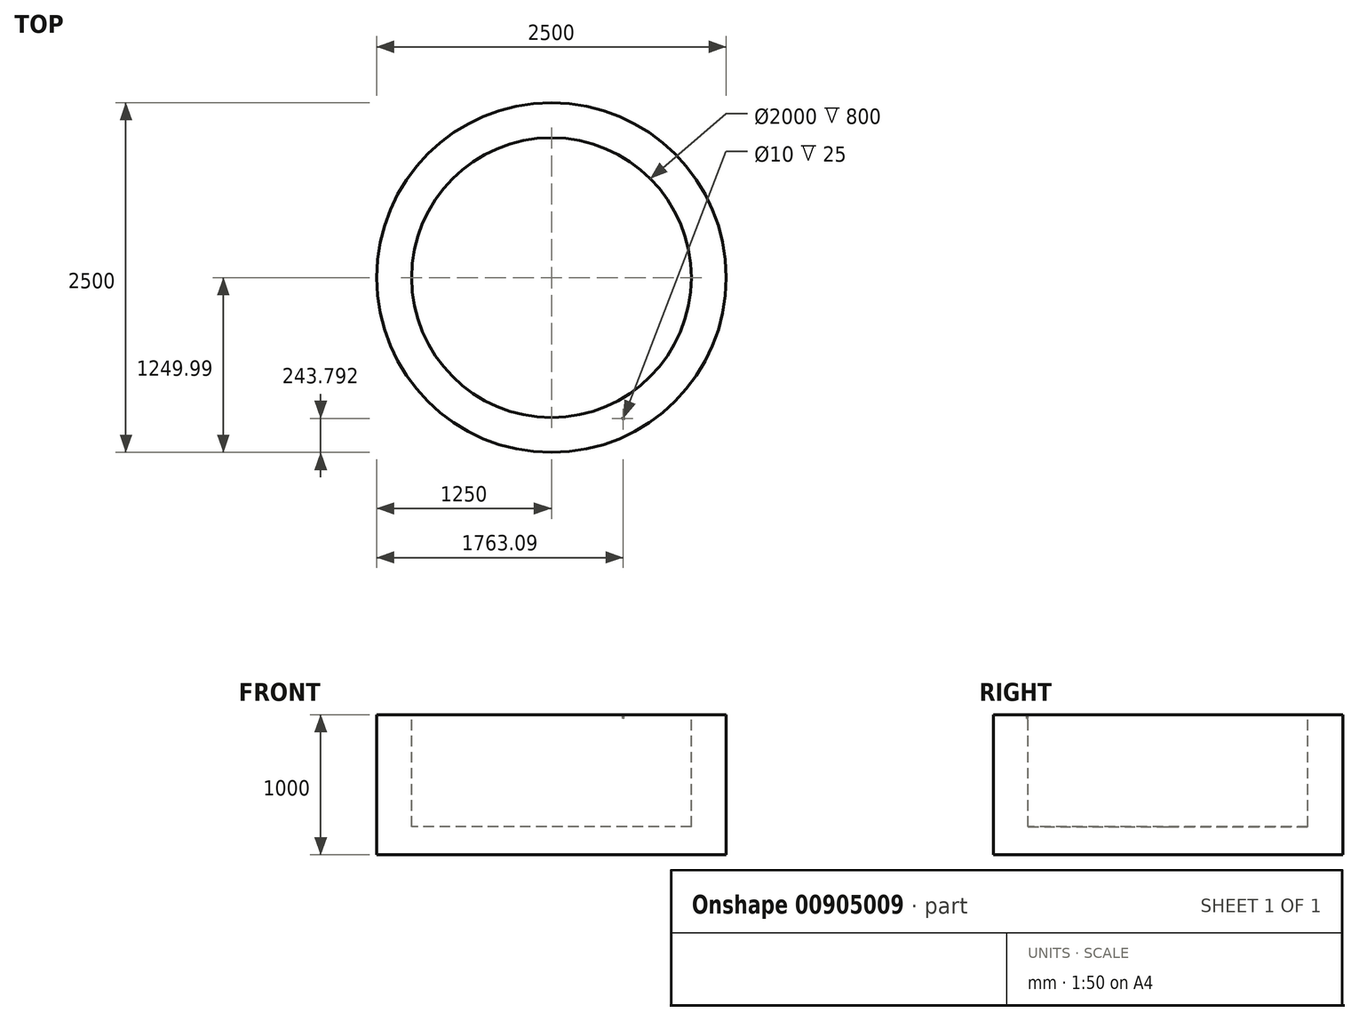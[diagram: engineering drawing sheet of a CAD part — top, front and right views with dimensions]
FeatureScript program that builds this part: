
annotation { "Feature Type Name" : "Feature", "Feature Type Description" : "" }
export const myFeature = defineFeature(function(context is Context, id is Id, definition is map)
    precondition{}
    {
        {
            var Q0;
            Q0=qCreatedBy(makeId("Top.planeOp"),FACE);
            var sketch = newSketch(context, id + "F0", { "sketchPlane" : qUnion([Q0])});
            skCircle(sketch, "E0", {"center": v(-2.06, 1.92) * mm, "radius": 1250 * mm});
            skSolve(sketch);
        }
        {
            var Q0;
            Q0 = qSketchRegion(id + "F0", true);
            extrude(context, id + "F1", {"entities" : qUnion([Q0]), "depth" : 1000 * mm, "offsetDistance" : 25.4 * mm});
        }
        {
            var Q0;
            Q0=makeQuery(id+"F1.opExtrude","CAP_FACE",FACE,{"disambiguationData":[OSD([sQuery(id+"F0.wireOp",EDGE,"E0")])],"isStart":false});
            var sketch = newSketch(context, id + "F2", { "sketchPlane" : qUnion([Q0])});
            skCircle(sketch, "E1", {"center": v(-2.06, 1.92) * mm, "radius": 1000 * mm});
            skSolve(sketch);
        }
        {
            var Q0;
            Q0=makeQuery(id+"F2.imprint","IMPRINT",FACE,{"disambiguationData":[TD([[makeQuery(id+"F2.imprint","IMPRINT",EDGE,{"derivedFrom":sQuery(id+"F2.wireOp",EDGE,"E1")}),1.0]])]});
            extrude(context, id + "F3", {"entities" : qUnion([Q0]), "operationType" : NewBodyOperationType.REMOVE, "oppositeDirection" : true, "depth" : 800 * mm, "offsetDistance" : 25 * mm});
        }
        {
            var Q0;
            Q0=makeQuery(id+"F1.opExtrude","CAP_FACE",FACE,{"disambiguationData":[OSD([sQuery(id+"F0.wireOp",EDGE,"E0")])],"isStart":false});
            var sketch = newSketch(context, id + "F4", { "sketchPlane" : qUnion([Q0])});
            skSolve(sketch);
        }
        {
            var Q0;
            Q0=makeQuery(id+"F4.imprint","IMPRINT",FACE,{"disambiguationData":[TD([[makeQuery(id+"F4.imprint","IMPRINT",EDGE,{"derivedFrom":makeQuery(id+"F1.opExtrude","CAP_EDGE",EDGE,{"disambiguationData":[OSD([sQuery(id+"F0.wireOp",EDGE,"E0")])],"isStart":false})}),1.0]])]});
            var sketch = newSketch(context, id + "F5", { "sketchPlane" : qUnion([Q0])});
            skCircle(sketch, "E2", {"center": v(511.03, -1004.29) * mm, "radius": 5 * mm});
            skSolve(sketch);
        }
        {
            var Q0;
            Q0=makeQuery(id+"F5.imprint","IMPRINT",FACE,{"disambiguationData":[TD([[makeQuery(id+"F5.imprint","IMPRINT",EDGE,{"derivedFrom":sQuery(id+"F5.wireOp",EDGE,"E2")}),1.0]])]});
            extrude(context, id + "F6", {"entities" : qUnion([Q0]), "operationType" : NewBodyOperationType.REMOVE, "oppositeDirection" : true, "depth" : 25 * mm, "offsetDistance" : 25 * mm});
        }
    });
